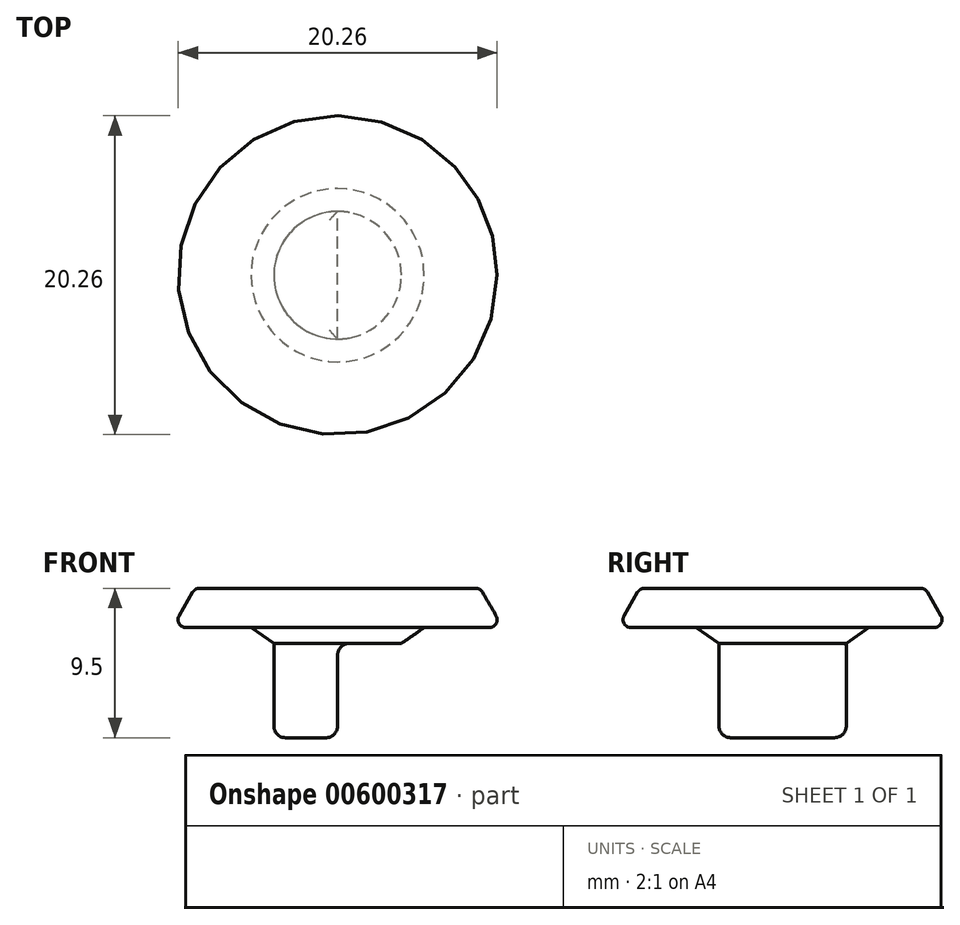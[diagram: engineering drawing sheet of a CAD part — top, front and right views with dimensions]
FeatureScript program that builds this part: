
annotation { "Feature Type Name" : "Feature", "Feature Type Description" : "" }
export const myFeature = defineFeature(function(context is Context, id is Id, definition is map)
    precondition{}
    {
        {
            var Q0;
            Q0=qCreatedBy(makeId("Front.planeOp"),FACE);
            var sketch = newSketch(context, id + "F0", { "sketchPlane" : qUnion([Q0])});
            skLineSegment(sketch, "E0", {"start": v(4.05, 6) * mm, "end": v(5.5, 7) * mm});
            skLineSegment(sketch, "E1", {"start": v(5.5, 7) * mm, "end": v(10.5, 7) * mm});
            skLineSegment(sketch, "E2", {"start": v(0, 9.5) * mm, "end": v(0, 0) * mm});
            skLineSegment(sketch, "E3", {"start": v(4.05, 6) * mm, "end": v(4.05, 0) * mm});
            skLineSegment(sketch, "E4", {"start": v(4.05, 0) * mm, "end": v(0, 0) * mm});
            skPoint(sketch, "E5.orphan", {"position": v(0, 0) * mm});
            skLineSegment(sketch, "E6", {"start": v(10.5, 7) * mm, "end": v(9.06, 9.5) * mm});
            skLineSegment(sketch, "E7", {"start": v(9.06, 9.5) * mm, "end": v(0, 9.5) * mm});
            skSolve(sketch);
        }
        {
            var Q0;
            Q0=qSketchRegion(id+"F0",true);
            var Q1;
            Q1=sQuery(id+"F0.wireOp",EDGE,"E2");
            revolve(context, id + "F1", {"entities" : qUnion([Q0]), "axis" : qUnion([Q1]), "revolveType" : RevolveType.FULL});
        }
        {
            var Q0;
            Q0=makeQuery(id+"F1.opRevolve","SWEPT_FACE",FACE,{"disambiguationData":[OSD([sQuery(id+"F0.wireOp",EDGE,"E4")])]});
            var sketch = newSketch(context, id + "F2", { "sketchPlane" : qUnion([Q0])});
            skLineSegment(sketch, "E8.bottom", {"start": v(0, 4.05) * mm, "end": v(4.05, 4.05) * mm});
            skLineSegment(sketch, "E8.top", {"start": v(0, -4.05) * mm, "end": v(4.05, -4.05) * mm});
            skLineSegment(sketch, "E8.left", {"start": v(0, 4.05) * mm, "end": v(0, -4.05) * mm});
            skLineSegment(sketch, "E8.right", {"start": v(4.05, 4.05) * mm, "end": v(4.05, -4.05) * mm});
            skSolve(sketch);
        }
        {
            var Q0;
            Q0 = qSketchRegion(id + "F2", true);
            var Q1;
            Q1=makeQuery(id+"F1.opRevolve","SWEPT_FACE",FACE,{"disambiguationData":[OSD([sQuery(id+"F0.wireOp",EDGE,"36Q2A1E8-CaD5-0Jy8-XmEI-qCisEAcXPKzw")])]});
            extrude(context, id + "F3", {"entities" : qUnion([Q0]), "operationType" : NewBodyOperationType.REMOVE, "oppositeDirection" : true, "depth" : 6 * mm, "endBoundEntityFace" : qUnion([Q1]), "offsetDistance" : 25 * mm});
        }
        {
            var Q0;
            {var subQ2=makeQuery(id+"F2R5GIXbNTLPHZD_2.boolean.opBoolean","COPY",FACE,{"derivedFrom":makeQuery(id+"F2R5GIXbNTLPHZD_2.opExtrude","SWEPT_FACE",FACE,{"disambiguationData":[OSD([sQuery(id+"F2.wireOp",EDGE,"6RF5FfAt-YfcN-XYpJ-voTT-JPPEjn318RsV")])]})});Q0=makeQuery(id+"Fmqv6moUgZnORJw_2.2.F2R5GIXbNTLPHZD_2.boolean.opBoolean","SPLIT",FACE,{"disambiguationData":[TD([subQ2])],"derivedFrom":makeQuery(id+"Fmqv6moUgZnORJw_2.1.F2R5GIXbNTLPHZD_2.boolean.opBoolean","SPLIT",FACE,{"disambiguationData":[TD([subQ2])],"derivedFrom":makeQuery(id+"F1.opRevolve","SWEPT_FACE",FACE,{"disambiguationData":[OSD([sQuery(id+"F0.wireOp",EDGE,"E4")])]})})});}
            var Q1;
            {var subQ1=makeQuery(id+"Fmqv6moUgZnORJw_2.1.F2R5GIXbNTLPHZD_2.opExtrude","SWEPT_FACE",FACE,{"disambiguationData":[OSD([sQuery(id+"F2.wireOp",EDGE,"kqsyaNb8-ErKI-FfWI-nr5y-aiWRytRq8sQ2")])]});var subQ3=sQuery(id+"F2.wireOp",EDGE,"6RF5FfAt-YfcN-XYpJ-voTT-JPPEjn318RsV");Q1=makeQuery(id+"Fmqv6moUgZnORJw_2.2.F2R5GIXbNTLPHZD_2.boolean.opBoolean","SPLIT",FACE,{"disambiguationData":[TD([makeQuery(id+"Fmqv6moUgZnORJw_2.1.F2R5GIXbNTLPHZD_2.boolean.opBoolean","COPY",FACE,{"derivedFrom":subQ1})])],"derivedFrom":makeQuery(id+"Fmqv6moUgZnORJw_2.1.F2R5GIXbNTLPHZD_2.boolean.opBoolean","SPLIT",FACE,{"disambiguationData":[TD([makeQuery(id+"F2R5GIXbNTLPHZD_2.boolean.opBoolean","COPY",FACE,{"derivedFrom":makeQuery(id+"F2R5GIXbNTLPHZD_2.opExtrude","SWEPT_FACE",FACE,{"disambiguationData":[OSD([subQ3])]})})])],"derivedFrom":makeQuery(id+"F1.opRevolve","SWEPT_FACE",FACE,{"disambiguationData":[OSD([sQuery(id+"F0.wireOp",EDGE,"E4")])]})})});}
            var Q2;
            Q2=makeQuery(id+"Fmqv6moUgZnORJw_2.1.F2R5GIXbNTLPHZD_2.boolean.opBoolean","SPLIT",FACE,{"disambiguationData":[TD([makeQuery(id+"F2R5GIXbNTLPHZD_2.boolean.opBoolean","COPY",FACE,{"derivedFrom":makeQuery(id+"F2R5GIXbNTLPHZD_2.opExtrude","SWEPT_FACE",FACE,{"disambiguationData":[OSD([sQuery(id+"F2.wireOp",EDGE,"kqsyaNb8-ErKI-FfWI-nr5y-aiWRytRq8sQ2")])]})})])],"derivedFrom":makeQuery(id+"F1.opRevolve","SWEPT_FACE",FACE,{"disambiguationData":[OSD([sQuery(id+"F0.wireOp",EDGE,"E4")])]})});
            var Q3;
            Q3=makeQuery(id+"F3.boolean.opBoolean","COPY",EDGE,{"derivedFrom":makeQuery(id+"F3.opExtrude","CAP_EDGE",EDGE,{"disambiguationData":[OSD([sQuery(id+"F2.wireOp",EDGE,"E8.left")])],"isStart":false})});
            fillet(context, id + "F4", {"entities" : qUnion([Q0, Q1, Q2, Q3]), "radius" : .75 * mm, "tangentPropagation" : true, "allowEdgeOverflow" : false});
        }
        {
            var Q0;
            Q0=makeQuery(id+"F1.opRevolve","SWEPT_EDGE",EDGE,{"disambiguationData":[OSD([sQuery(id+"F0.wireOp",EDGE,"E6"),sQuery(id+"F0.wireOp",EDGE,"E7")])]});
            var Q1;
            Q1=makeQuery(id+"F1.opRevolve","SWEPT_EDGE",EDGE,{"disambiguationData":[OSD([sQuery(id+"F0.wireOp",EDGE,"E1"),sQuery(id+"F0.wireOp",EDGE,"E6")])]});
            fillet(context, id + "F5", {"entities" : qUnion([Q0, Q1]), "radius" : .5 * mm, "tangentPropagation" : true, "allowEdgeOverflow" : false});
        }
    });
